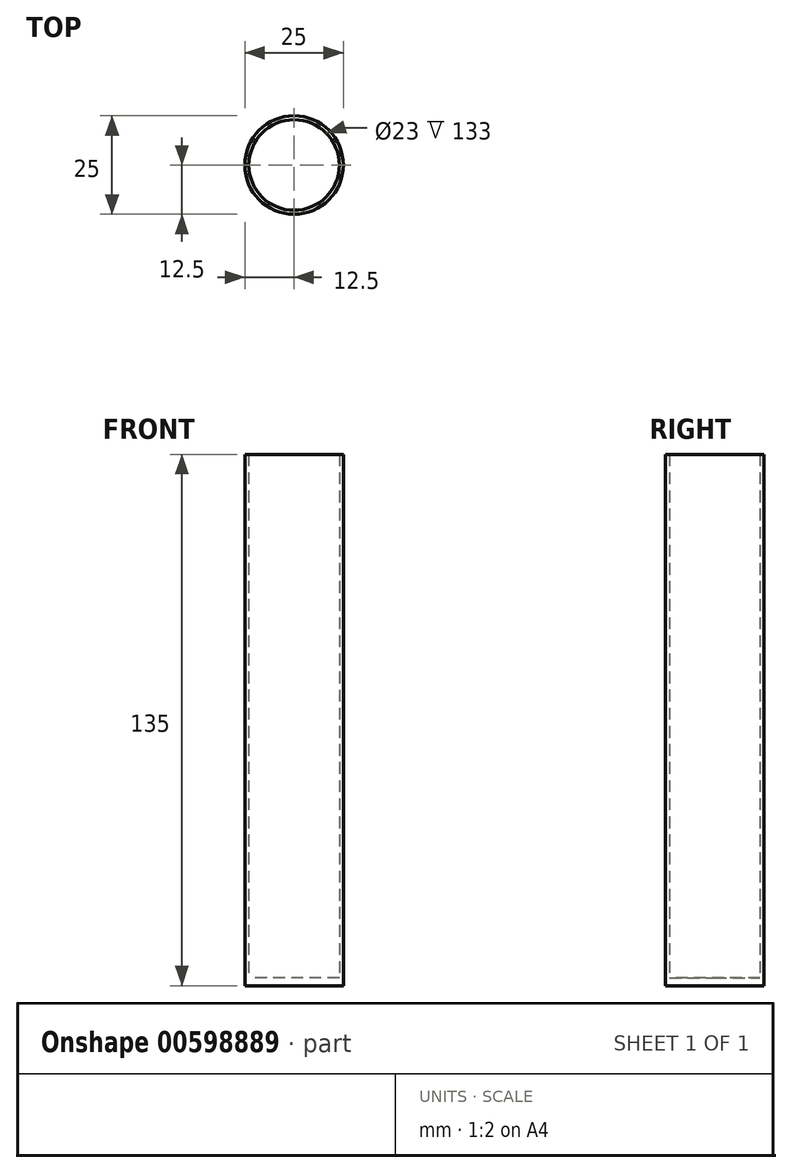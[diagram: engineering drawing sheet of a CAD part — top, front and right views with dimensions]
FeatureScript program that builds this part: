
annotation { "Feature Type Name" : "Feature", "Feature Type Description" : "" }
export const myFeature = defineFeature(function(context is Context, id is Id, definition is map)
    precondition{}
    {
        {
            var Q0;
            Q0=qCreatedBy(makeId("Top.planeOp"),FACE);
            var sketch = newSketch(context, id + "F0", { "sketchPlane" : qUnion([Q0])});
            skCircle(sketch, "E0", {"center": v(0, 0) * mm, "radius": 12.5 * mm});
            skSolve(sketch);
        }
        {
            var Q0;
            Q0=qSketchRegion(id+"F0",true);
            extrude(context, id + "F1", {"entities" : qUnion([Q0]), "depth" : 2 * mm, "offsetDistance" : 25 * mm});
        }
        {
            var Q0;
            Q0=makeQuery(id+"F1.opExtrude","CAP_FACE",FACE,{"disambiguationData":[OSD([sQuery(id+"F0.wireOp",EDGE,"E0")])],"isStart":false});
            var sketch = newSketch(context, id + "F2", { "sketchPlane" : qUnion([Q0])});
            skCircle(sketch, "E1", {"center": v(0, 0) * mm, "radius": 11.5 * mm});
            skSolve(sketch);
        }
        {
            var Q0;
            Q0=makeQuery(id+"F2.imprint","IMPRINT",FACE,{"disambiguationData":[TD([[makeQuery(id+"F2.imprint","IMPRINT",EDGE,{"derivedFrom":sQuery(id+"F2.wireOp",EDGE,"E1")}),-1.0]])]});
            extrude(context, id + "F3", {"entities" : qUnion([Q0]), "operationType" : NewBodyOperationType.ADD, "depth" : 133 * mm, "offsetDistance" : 25 * mm});
        }
    });
